# Revit family: Wall_Hung _Multiple_Station_Hand_Wash_Sink_kit-Elkay-EWMA6020_SACTMC_SACC
name_source: partatom
category: Plumbing Fixtures
units: mm (PartAtom-declared; Revit-internal decimal feet)

## family parameters
Cut with Voids When Loaded = No
Host = Face
Maintain Annotation Orientation = No
OmniClass Number = 23.45.05.14.14
OmniClass Title = Sinks/Lavatories
Part Type = Normal
Room Calculation Point = No
Round Connector Dimension = Use Diameter
Shared = No

## types (2) — shared parameters
Assembly Code = D2010400
Back splash Height = 10.00"
Back splash width = 2.00"
Bowl  Dimensions = 57 inch x 16 1/2 inch x 8 inch
Bowl Width = 16.50"
Bowl length = 57.00"
C/C distance of Center2-Hole pair holes = 40.00"
CL of Hole = 3.50"
Center 2-Hole pair = Yes
Default Elevation = 48.00"
Drain Location = Center
Drain Location along y-axis = 6.88"
Front rim = 1.50"
Guage = 14
Inlet Connection Size (inch) = 0.50"
Installation type = Wall Hung
Main Material = Finish-Elkay-Stainless Steel
Manufacturer = Elkay Manufacturer Company
Manufacturer Brand = Elkay (by Zurn Elkay Water Solutions)
No of Bowls = 1
Outlet Connection Size (inch) = 1.50"
Product Documentation Link = https://www.elkayfiles.com
Product Installation Sheet URL = https://www.elkayfiles.com
Product Page URL = https://www.elkay.com
Product Weight (lbs) = 114
Product data URL = https://www.bimobject.com
Repair Parts URL = https://www.elkayfiles.com
Rim = 1.50"
Sink Depth = 18.00"
Sink Dimensions = 60 inch x 20 inch x 18 inch
Sink Length = 60.00"
Sink Width = 20.00"
URL = https://www.elkay.com
center Hole = Yes

## per-type parameters (varying)
| type | Approx. Shipping Weight (lbs) | Description | Drain Location along x-axis | Drain Size | Model | Thermostatic Mixing valve |
| EWMA6020SACTMC (Wall Hung Multiple Station Sink kit) | 122 | Stainless Steel 60 inch x 20 inch x 18 inch 6- Wall Hung Multiple Station Hand Wash Sink Kit w/Faucets +Drain+Thermostatic Mixing Valves | 30.00" | 3 1/2 inch | EWMA6020SACTMC | Yes |
| EWMA6020SACC (Wall Hung Multiple Station Sink kit) | 116 | Stainless Steel 60 inch x 20 inch x 18 inch Wall Hung Multiple Station Hand Wash Sink Kit w/Faucets +Drain | 22.50" | 3 1/2 | EWMA6020SACC | No |

## geometry (parser evidence)
native form markers: Sweep x12
no freeform markers — native parametric forms only
